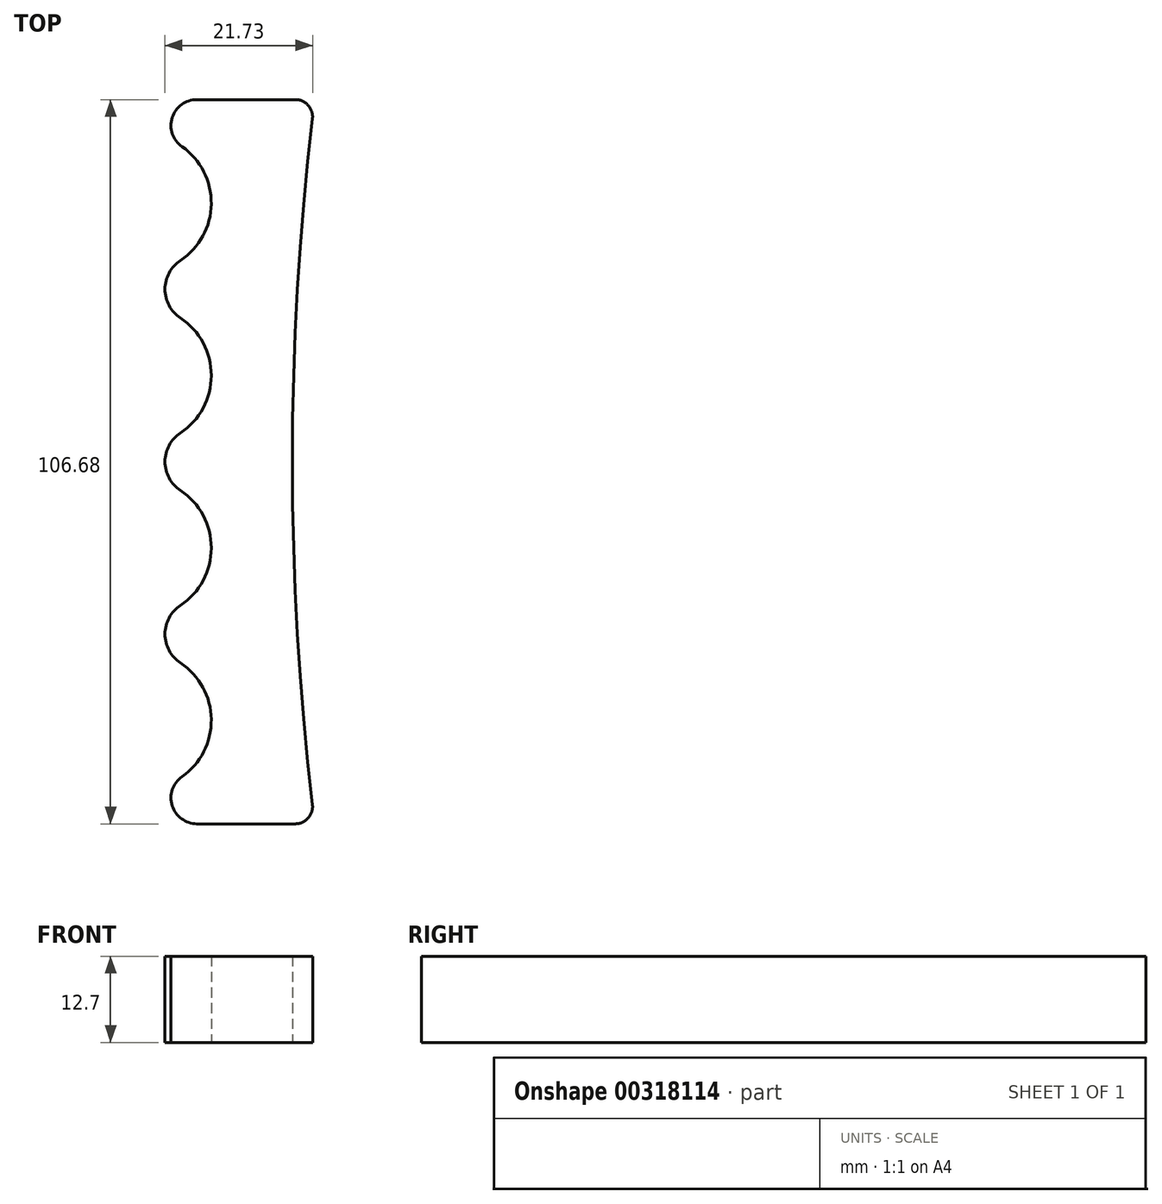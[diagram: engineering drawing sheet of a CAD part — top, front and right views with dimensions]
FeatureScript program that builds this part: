
annotation { "Feature Type Name" : "Feature", "Feature Type Description" : "" }
export const myFeature = defineFeature(function(context is Context, id is Id, definition is map)
    precondition{}
    {
        {
            var Q0;
            Q0=qCreatedBy(makeId("Top.planeOp"),FACE);
            var sketch = newSketch(context, id + "F0", { "sketchPlane" : qUnion([Q0])});
            skLineSegment(sketch, "E0", {"start": v(7.7, 54.56) * mm, "end": v(-15.16, 54.56) * mm});
            skLineSegment(sketch, "E1", {"start": v(10.24, -52.12) * mm, "end": v(-15.16, -52.12) * mm});
            skLineSegment(sketch, "E2", {"start": v(-15.16, 54.56) * mm, "end": v(-15.16, 49.48) * mm});
            skArc(sketch, "E3", {"start": v(-15.16, -21.64) * mm, "mid": v(-5, -11.48) * mm, "end": v(-15.16, -1.32) * mm});
            skArc(sketch, "E4", {"start": v(-15.16, 3.76) * mm, "mid": v(-5, 13.92) * mm, "end": v(-15.16, 24.08) * mm});
            skArc(sketch, "E5", {"start": v(-15.16, 29.16) * mm, "mid": v(-5, 39.32) * mm, "end": v(-15.16, 49.48) * mm});
            skLineSegment(sketch, "E6.trimOffspring", {"start": v(-15.16, 29.16) * mm, "end": v(-15.16, 24.08) * mm});
            skLineSegment(sketch, "E7.trimOffspring", {"start": v(-15.16, 3.76) * mm, "end": v(-15.16, -1.32) * mm});
            skLineSegment(sketch, "E8.trimOffspring", {"start": v(-15.16, -21.64) * mm, "end": v(-15.16, -26.72) * mm});
            skLineSegment(sketch, "E9.trimOffspring", {"start": v(-15.16, -47.04) * mm, "end": v(-15.16, -52.12) * mm});
            skArc(sketch, "E10", {"start": v(-15.16, -47.04) * mm, "mid": v(-5, -36.88) * mm, "end": v(-15.16, -26.72) * mm});
            skPoint(sketch, "E11.visualSharp", {"position": v(10.24, 54.56) * mm});
            skPoint(sketch, "E12.visualSharp", {"position": v(10.24, -52.12) * mm});
            skArc(sketch, "E13", {"start": v(10.24, 54.56) * mm, "mid": v(6.94, 1.22) * mm, "end": v(10.24, -52.12) * mm});
            skLineSegment(sketch, "E14", {"start": v(7.7, 54.56) * mm, "end": v(10.24, 54.56) * mm});
            skSolve(sketch);
        }
        {
            var Q0;
            Q0 = qSketchRegion(id + "F0", true);
            extrude(context, id + "F1", {"entities" : qUnion([Q0]), "depth" : 12.7 * mm});
        }
        {
            var Q0;
            Q0=makeQuery(id+"F1.opExtrude","SWEPT_EDGE",EDGE,{"disambiguationData":[OSD([sQuery(id+"F0.wireOp",EDGE,"E8.trimOffspring"),sQuery(id+"F0.wireOp",EDGE,"E10")])]});
            var Q1;
            Q1=makeQuery(id+"F1.opExtrude","SWEPT_EDGE",EDGE,{"disambiguationData":[OSD([sQuery(id+"F0.wireOp",EDGE,"E3"),sQuery(id+"F0.wireOp",EDGE,"E8.trimOffspring")])]});
            fillet(context, id + "F2", {"entities" : qUnion([Q0, Q1]), "radius" : 3.8 * mm, "tangentPropagation" : true, "allowEdgeOverflow" : false});
        }
        {
            var Q0;
            {var subQ0=sQuery(id+"F0.wireOp",EDGE,"E8.trimOffspring");Q0=makeQuery(id+"F2.opFillet","BLEND_EDGE",EDGE,{"blendedFrom":[makeQuery(id+"F1.opExtrude","SWEPT_EDGE",EDGE,{"disambiguationData":[OSD([sQuery(id+"F0.wireOp",EDGE,"E3"),subQ0])]}),makeQuery(id+"F1.opExtrude","SWEPT_EDGE",EDGE,{"disambiguationData":[OSD([subQ0,sQuery(id+"F0.wireOp",EDGE,"E10")])]})],"blendedInto":[]});}
            fillet(context, id + "F3", {"entities" : qUnion([Q0]), "radius" : 5.08 * mm, "tangentPropagation" : true, "allowEdgeOverflow" : false});
        }
        {
            var Q0;
            Q0=makeQuery(id+"F1.opExtrude","SWEPT_EDGE",EDGE,{"disambiguationData":[OSD([sQuery(id+"F0.wireOp",EDGE,"E5"),sQuery(id+"F0.wireOp",EDGE,"E6.trimOffspring")])]});
            var Q1;
            Q1=makeQuery(id+"F1.opExtrude","SWEPT_EDGE",EDGE,{"disambiguationData":[OSD([sQuery(id+"F0.wireOp",EDGE,"E4"),sQuery(id+"F0.wireOp",EDGE,"E7.trimOffspring")])]});
            var Q2;
            Q2=makeQuery(id+"F1.opExtrude","SWEPT_EDGE",EDGE,{"disambiguationData":[OSD([sQuery(id+"F0.wireOp",EDGE,"E3"),sQuery(id+"F0.wireOp",EDGE,"E7.trimOffspring")])]});
            var Q3;
            Q3=makeQuery(id+"F1.opExtrude","SWEPT_EDGE",EDGE,{"disambiguationData":[OSD([sQuery(id+"F0.wireOp",EDGE,"E4"),sQuery(id+"F0.wireOp",EDGE,"E6.trimOffspring")])]});
            fillet(context, id + "F4", {"entities" : qUnion([Q0, Q1, Q2, Q3]), "radius" : 3.8 * mm, "tangentPropagation" : true, "allowEdgeOverflow" : false});
        }
        {
            var Q0;
            {var subQ0=sQuery(id+"F0.wireOp",EDGE,"E6.trimOffspring");Q0=makeQuery(id+"F4.opFillet","BLEND_EDGE",EDGE,{"blendedFrom":[makeQuery(id+"F1.opExtrude","SWEPT_EDGE",EDGE,{"disambiguationData":[OSD([sQuery(id+"F0.wireOp",EDGE,"E4"),subQ0])]}),makeQuery(id+"F1.opExtrude","SWEPT_EDGE",EDGE,{"disambiguationData":[OSD([sQuery(id+"F0.wireOp",EDGE,"E5"),subQ0])]})],"blendedInto":[]});}
            var Q1;
            {var subQ0=sQuery(id+"F0.wireOp",EDGE,"E7.trimOffspring");Q1=makeQuery(id+"F4.opFillet","BLEND_EDGE",EDGE,{"blendedFrom":[makeQuery(id+"F1.opExtrude","SWEPT_EDGE",EDGE,{"disambiguationData":[OSD([sQuery(id+"F0.wireOp",EDGE,"E3"),subQ0])]}),makeQuery(id+"F1.opExtrude","SWEPT_EDGE",EDGE,{"disambiguationData":[OSD([sQuery(id+"F0.wireOp",EDGE,"E4"),subQ0])]})],"blendedInto":[]});}
            fillet(context, id + "F5", {"entities" : qUnion([Q0, Q1]), "radius" : 5.08 * mm, "tangentPropagation" : true, "allowEdgeOverflow" : false});
        }
        {
            var Q0;
            Q0=makeQuery(id+"F1.opExtrude","SWEPT_EDGE",EDGE,{"disambiguationData":[OSD([sQuery(id+"F0.wireOp",EDGE,"E0"),sQuery(id+"F0.wireOp",EDGE,"E2")])]});
            fillet(context, id + "F6", {"entities" : qUnion([Q0]), "radius" : 6.35 * mm, "tangentPropagation" : true, "allowEdgeOverflow" : false});
        }
        {
            var Q0;
            Q0=makeQuery(id+"F6.opFillet","BLEND_EDGE",EDGE,{"blendedFrom":[makeQuery(id+"F1.opExtrude","SWEPT_EDGE",EDGE,{"disambiguationData":[OSD([sQuery(id+"F0.wireOp",EDGE,"E0"),sQuery(id+"F0.wireOp",EDGE,"E2")])]}),makeQuery(id+"F1.opExtrude","SWEPT_FACE",FACE,{"disambiguationData":[OSD([sQuery(id+"F0.wireOp",EDGE,"E5")])]})],"blendedInto":[makeQuery(id+"F1.opExtrude","SWEPT_FACE",FACE,{"disambiguationData":[OSD([sQuery(id+"F0.wireOp",EDGE,"E5")])]})]});
            fillet(context, id + "F7", {"entities" : qUnion([Q0]), "radius" : 3.8 * mm, "tangentPropagation" : true, "allowEdgeOverflow" : false});
        }
        {
            var Q0;
            Q0=makeQuery(id+"F1.opExtrude","SWEPT_EDGE",EDGE,{"disambiguationData":[OSD([sQuery(id+"F0.wireOp",EDGE,"E1"),sQuery(id+"F0.wireOp",EDGE,"E9.trimOffspring")])]});
            fillet(context, id + "F8", {"entities" : qUnion([Q0]), "radius" : 6.35 * mm, "tangentPropagation" : true, "allowEdgeOverflow" : false});
        }
        {
            var Q0;
            Q0=makeQuery(id+"F8.opFillet","BLEND_EDGE",EDGE,{"blendedFrom":[makeQuery(id+"F1.opExtrude","SWEPT_EDGE",EDGE,{"disambiguationData":[OSD([sQuery(id+"F0.wireOp",EDGE,"E1"),sQuery(id+"F0.wireOp",EDGE,"E9.trimOffspring")])]}),makeQuery(id+"F1.opExtrude","SWEPT_FACE",FACE,{"disambiguationData":[OSD([sQuery(id+"F0.wireOp",EDGE,"E10")])]})],"blendedInto":[makeQuery(id+"F1.opExtrude","SWEPT_FACE",FACE,{"disambiguationData":[OSD([sQuery(id+"F0.wireOp",EDGE,"E10")])]})]});
            fillet(context, id + "F9", {"entities" : qUnion([Q0]), "radius" : 3.8 * mm, "tangentPropagation" : true, "allowEdgeOverflow" : false});
        }
        {
            var Q0;
            Q0=makeQuery(id+"F1.opExtrude","SWEPT_EDGE",EDGE,{"disambiguationData":[OSD([sQuery(id+"F0.wireOp",EDGE,"E13"),sQuery(id+"F0.wireOp",EDGE,"E14")])]});
            var Q1;
            Q1=makeQuery(id+"F1.opExtrude","SWEPT_EDGE",EDGE,{"disambiguationData":[OSD([sQuery(id+"F0.wireOp",EDGE,"E13"),sQuery(id+"F0.wireOp",EDGE,"TSZq3QvV-2R6O-UcTB-i5TT-7QcYFSYoz1f6")])]});
            fillet(context, id + "F10", {"entities" : qUnion([Q0, Q1]), "radius" : 2.54 * mm, "tangentPropagation" : true, "allowEdgeOverflow" : false});
        }
    });
